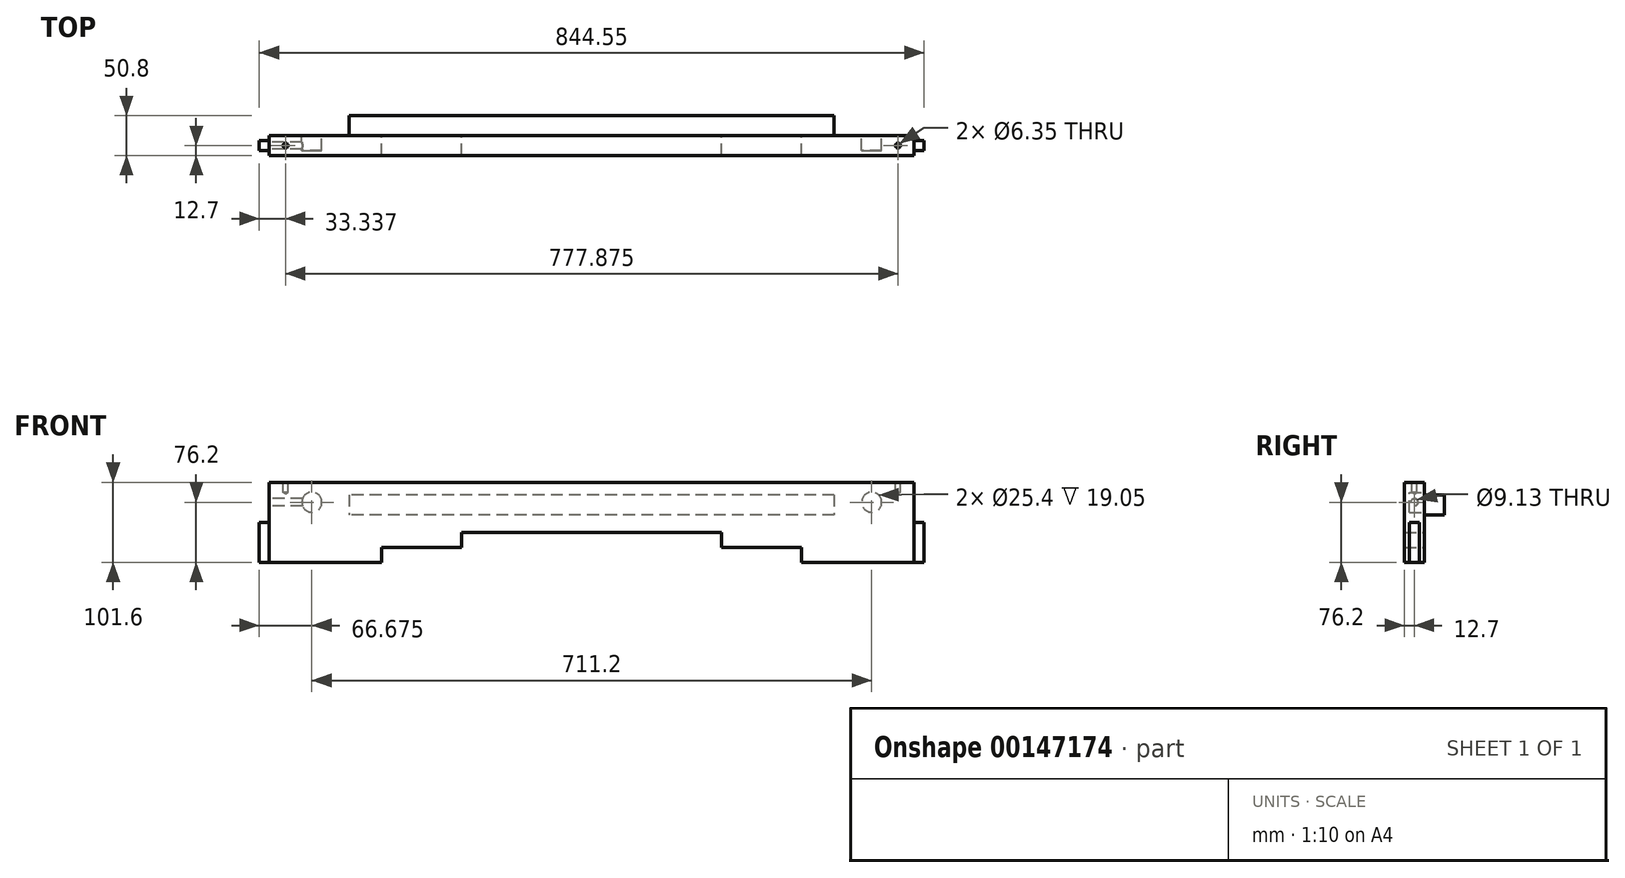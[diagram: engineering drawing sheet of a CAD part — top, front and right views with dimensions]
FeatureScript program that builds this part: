
annotation { "Feature Type Name" : "Feature", "Feature Type Description" : "" }
export const myFeature = defineFeature(function(context is Context, id is Id, definition is map)
    precondition{}
    {
        {
            var Q0;
            Q0=qCreatedBy(makeId("Front.planeOp"),FACE);
            var sketch = newSketch(context, id + "F0", { "sketchPlane" : qUnion([Q0])});
            skLineSegment(sketch, "E0.bottom", {"start": v(0, 0) * mm, "end": v(819.15, 0) * mm});
            skLineSegment(sketch, "E0.top", {"start": v(0, 101.6) * mm, "end": v(819.15, 101.6) * mm});
            skLineSegment(sketch, "E0.left", {"start": v(0, 0) * mm, "end": v(0, 101.6) * mm});
            skLineSegment(sketch, "E0.right", {"start": v(819.15, 0) * mm, "end": v(819.15, 101.6) * mm});
            skSolve(sketch);
        }
        {
            var Q0;
            Q0=makeQuery(id+"F0.imprint","IMPRINT",FACE,{"disambiguationData":[TD([[makeQuery(id+"F0.imprint","IMPRINT",EDGE,{"derivedFrom":sQuery(id+"F0.wireOp",EDGE,"E0.bottom")}),1.0]])]});
            extrude(context, id + "F1", {"entities" : qUnion([Q0]), "flatOperationType" : FlatOperationType.REMOVE, "depth" : 25.4 * mm, "offsetDistance" : 25.4 * mm, "domain" : OperationDomain.MODEL});
        }
        {
            var Q0;
            Q0=makeQuery(id+"F1.opExtrude","SWEPT_FACE",FACE,{"disambiguationData":[OSD([sQuery(id+"F0.wireOp",EDGE,"E0.left")])]});
            var sketch = newSketch(context, id + "F2", { "sketchPlane" : qUnion([Q0])});
            skLineSegment(sketch, "E1", {"start": v(12.7, 101.6) * mm, "end": v(12.7, 0) * mm, "construction": true});
            skCircle(sketch, "E2", {"center": v(12.7, 76.2) * mm, "radius": 4.56 * mm});
            skSolve(sketch);
        }
        {
            var Q0;
            Q0=makeQuery(id+"F2.imprint","IMPRINT",FACE,{"disambiguationData":[TD([[makeQuery(id+"F2.imprint","IMPRINT",EDGE,{"derivedFrom":sQuery(id+"F2.wireOp",EDGE,"E2")}),1.0]])]});
            var Q1;
            Q1 = qSketchRegion(id + "F4", true);
            extrude(context, id + "F3", {"entities" : qUnion([Q0, Q1]), "operationType" : NewBodyOperationType.REMOVE, "oppositeDirection" : true, "depth" : 50.8 * mm});
        }
        {
            var Q0;
            Q0=qCreatedBy(makeId("Front.planeOp"),FACE);
            var sketch = newSketch(context, id + "F4", { "sketchPlane" : qUnion([Q0])});
            skCircle(sketch, "E3", {"center": v(53.98, 76.2) * mm, "radius": 12.7 * mm});
            skCircle(sketch, "E4", {"center": v(765.18, 76.2) * mm, "radius": 12.7 * mm});
            skSolve(sketch);
        }
        {
            var Q0;
            Q0=makeQuery(id+"F4.imprint","IMPRINT",FACE,{"disambiguationData":[TD([[makeQuery(id+"F4.imprint","IMPRINT",EDGE,{"derivedFrom":sQuery(id+"F4.wireOp",EDGE,"E4")}),1.0]])]});
            var Q1;
            Q1=makeQuery(id+"F4.imprint","IMPRINT",FACE,{"disambiguationData":[TD([[makeQuery(id+"F4.imprint","IMPRINT",EDGE,{"derivedFrom":sQuery(id+"F4.wireOp",EDGE,"E3")}),1.0]])]});
            extrude(context, id + "F5", {"entities" : qUnion([Q0, Q1]), "operationType" : NewBodyOperationType.REMOVE, "depth" : 19.05 * mm});
        }
        {
            var Q0;
            Q0=makeQuery(id+"F1.opExtrude","CAP_FACE",FACE,{"disambiguationData":[OSD([sQuery(id+"F0.wireOp",EDGE,"E0.bottom"),sQuery(id+"F0.wireOp",EDGE,"E0.top"),sQuery(id+"F0.wireOp",EDGE,"E0.left"),sQuery(id+"F0.wireOp",EDGE,"E0.right")])],"isStart":true});
            var sketch = newSketch(context, id + "F6", { "sketchPlane" : qUnion([Q0])});
            skLineSegment(sketch, "E5", {"start": v(-676.28, 0) * mm, "end": v(-676.28, 19.05) * mm});
            skLineSegment(sketch, "E6", {"start": v(-676.28, 19.05) * mm, "end": v(-574.68, 19.05) * mm});
            skLineSegment(sketch, "E7", {"start": v(-574.68, 19.05) * mm, "end": v(-574.68, 38.1) * mm});
            skLineSegment(sketch, "E8", {"start": v(-574.68, 38.1) * mm, "end": v(-244.47, 38.1) * mm});
            skLineSegment(sketch, "E9", {"start": v(-244.47, 38.1) * mm, "end": v(-244.47, 19.05) * mm});
            skLineSegment(sketch, "E10", {"start": v(-244.47, 19.05) * mm, "end": v(-142.88, 19.05) * mm});
            skLineSegment(sketch, "E11", {"start": v(-142.88, 19.05) * mm, "end": v(-142.88, 0) * mm});
            skLineSegment(sketch, "E12", {"start": v(-142.87, 0) * mm, "end": v(-676.28, 0) * mm});
            skSolve(sketch);
        }
        {
            var Q0;
            Q0=makeQuery(id+"F6.imprint","IMPRINT",FACE,{"disambiguationData":[TD([[makeQuery(id+"F6.imprint","IMPRINT",EDGE,{"derivedFrom":sQuery(id+"F6.wireOp",EDGE,"E5")}),-1.0]])]});
            extrude(context, id + "F7", {"entities" : qUnion([Q0]), "operationType" : NewBodyOperationType.REMOVE, "endBound" : BoundingType.UP_TO_NEXT, "oppositeDirection" : true, "depth" : 25.4 * mm});
        }
        {
            var Q0;
            Q0=makeQuery(id+"F1.opExtrude","SWEPT_FACE",FACE,{"disambiguationData":[OSD([sQuery(id+"F0.wireOp",EDGE,"E0.top")])]});
            var sketch = newSketch(context, id + "F8", { "sketchPlane" : qUnion([Q0])});
            skLineSegment(sketch, "E13", {"start": v(20.64, 0) * mm, "end": v(20.64, -25.4) * mm, "construction": true});
            skLineSegment(sketch, "E14", {"start": v(0, -12.7) * mm, "end": v(20.64, -12.7) * mm, "construction": true});
            skLineSegment(sketch, "E15", {"start": v(3.17, 0) * mm, "end": v(3.18, -25.4) * mm, "construction": true});
            skLineSegment(sketch, "E16", {"start": v(409.57, -25.4) * mm, "end": v(409.57, 0) * mm, "construction": true});
            skLineSegment(sketch, "E17", {"start": v(815.98, 0) * mm, "end": v(815.98, -25.4) * mm, "construction": true});
            skLineSegment(sketch, "E18", {"start": v(798.51, 0) * mm, "end": v(798.51, -25.4) * mm, "construction": true});
            skLineSegment(sketch, "E19", {"start": v(20.64, -12.7) * mm, "end": v(819.15, -12.7) * mm, "construction": true});
            skPoint(sketch, "E20", {"position": v(798.51, -12.7) * mm});
            skSolve(sketch);
        }
        {
            var Q0;
            Q0=sQuery(id+"F8.wireOp",VERTEX,"E14.end");
            var Q1;
            Q1=sQuery(id+"F8.wireOp",VERTEX,"E20");
            var Q2;
            Q2=makeQuery(id+"F1.opExtrude","SWEPT_BODY",BODY,{"disambiguationData":[OSD([sQuery(id+"F0.wireOp",EDGE,"E0.bottom"),sQuery(id+"F0.wireOp",EDGE,"E0.top"),sQuery(id+"F0.wireOp",EDGE,"E0.left"),sQuery(id+"F0.wireOp",EDGE,"E0.right")])]});
            hole(context, id + "F9", {"style" : HoleStyle.SIMPLE, "endStyle" : HoleEndStyle.BLIND, "holeDiameter" : 6.35 * mm, "holeDepth" : 12.7 * mm, "locations" : qUnion([Q0, Q1]), "scope" : qUnion([Q2])});
        }
        {
            var Q0;
            Q0=qCreatedBy(makeId("Top.planeOp"),FACE);
            var sketch = newSketch(context, id + "F10", { "sketchPlane" : qUnion([Q0])});
            skLineSegment(sketch, "E21.bottom", {"start": v(0, -19.05) * mm, "end": v(-12.7, -19.05) * mm});
            skLineSegment(sketch, "E21.top", {"start": v(0, -6.35) * mm, "end": v(-12.7, -6.35) * mm});
            skLineSegment(sketch, "E21.left", {"start": v(0, -19.05) * mm, "end": v(0, -6.35) * mm});
            skLineSegment(sketch, "E21.right", {"start": v(-12.7, -19.05) * mm, "end": v(-12.7, -6.35) * mm});
            skLineSegment(sketch, "E22.bottom", {"start": v(819.15, -6.35) * mm, "end": v(831.85, -6.35) * mm});
            skLineSegment(sketch, "E22.top", {"start": v(819.15, -19.05) * mm, "end": v(831.85, -19.05) * mm});
            skLineSegment(sketch, "E22.left", {"start": v(831.85, -6.35) * mm, "end": v(831.85, -19.05) * mm});
            skLineSegment(sketch, "E22.right", {"start": v(819.15, -6.35) * mm, "end": v(819.15, -19.05) * mm});
            skSolve(sketch);
        }
        {
            var Q0;
            Q0=makeQuery(id+"F10.imprint","IMPRINT",FACE,{"disambiguationData":[TD([[makeQuery(id+"F10.imprint","IMPRINT",EDGE,{"derivedFrom":sQuery(id+"F10.wireOp",EDGE,"E21.bottom")}),-1.0]])]});
            var Q1;
            Q1=makeQuery(id+"F10.imprint","IMPRINT",FACE,{"disambiguationData":[TD([[makeQuery(id+"F10.imprint","IMPRINT",EDGE,{"derivedFrom":sQuery(id+"F10.wireOp",EDGE,"E22.bottom")}),-1.0]])]});
            extrude(context, id + "F11", {"entities" : qUnion([Q0, Q1]), "operationType" : NewBodyOperationType.ADD, "depth" : 50.8 * mm});
        }
        {
            var Q0;
            Q0=makeQuery(id+"F1.opExtrude","CAP_FACE",FACE,{"disambiguationData":[OSD([sQuery(id+"F0.wireOp",EDGE,"E0.bottom"),sQuery(id+"F0.wireOp",EDGE,"E0.top"),sQuery(id+"F0.wireOp",EDGE,"E0.left"),sQuery(id+"F0.wireOp",EDGE,"E0.right")])],"isStart":true});
            var sketch = newSketch(context, id + "F12", { "sketchPlane" : qUnion([Q0])});
            skLineSegment(sketch, "E23.bottom", {"start": v(-717.55, 85.73) * mm, "end": v(-101.6, 85.73) * mm});
            skLineSegment(sketch, "E23.top", {"start": v(-717.55, 60.33) * mm, "end": v(-101.6, 60.33) * mm});
            skLineSegment(sketch, "E23.left", {"start": v(-717.55, 85.73) * mm, "end": v(-717.55, 60.33) * mm});
            skLineSegment(sketch, "E23.right", {"start": v(-101.6, 85.73) * mm, "end": v(-101.6, 60.33) * mm});
            skSolve(sketch);
        }
        {
            var Q0;
            Q0=makeQuery(id+"F12.imprint","IMPRINT",FACE,{"disambiguationData":[TD([[makeQuery(id+"F12.imprint","IMPRINT",EDGE,{"derivedFrom":sQuery(id+"F12.wireOp",EDGE,"E23.bottom")}),-1.0]])]});
            extrude(context, id + "F13", {"entities" : qUnion([Q0]), "operationType" : NewBodyOperationType.ADD, "depth" : 25.4 * mm});
        }
    });
